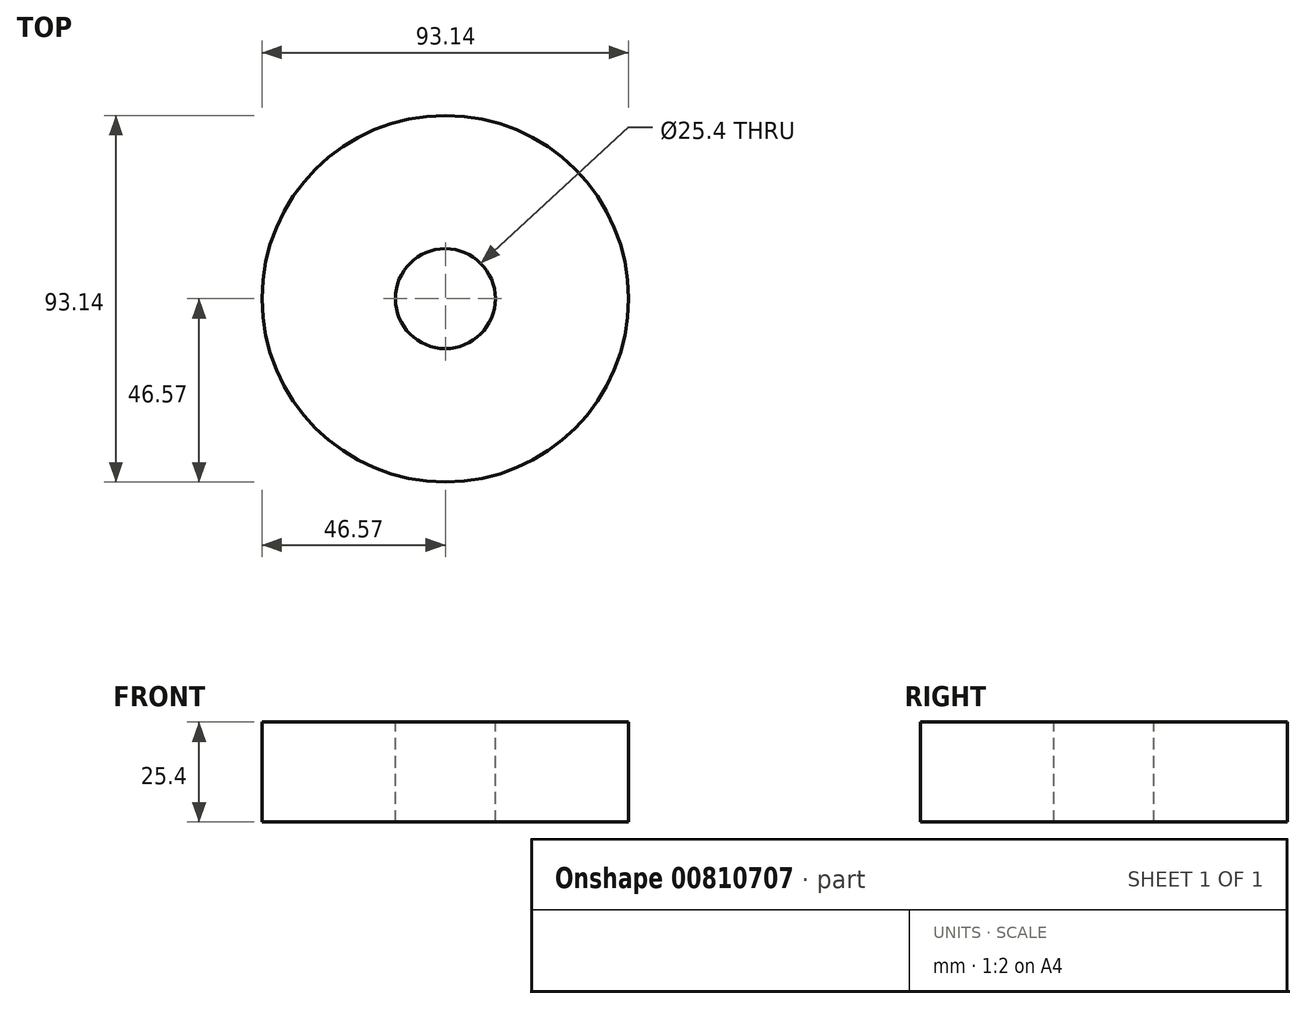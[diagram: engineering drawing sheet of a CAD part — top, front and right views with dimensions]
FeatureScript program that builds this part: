
annotation { "Feature Type Name" : "Feature", "Feature Type Description" : "" }
export const myFeature = defineFeature(function(context is Context, id is Id, definition is map)
    precondition{}
    {
        {
            var Q0;
            Q0=qCreatedBy(makeId("Top.planeOp"),FACE);
            var sketch = newSketch(context, id + "F0", { "sketchPlane" : qUnion([Q0])});
            skCircle(sketch, "E0", {"center": v(0, 0) * mm, "radius": 46.57 * mm});
            skSolve(sketch);
        }
        {
            var Q0;
            Q0 = qSketchRegion(id + "F0", true);
            extrude(context, id + "F1", {"entities" : qUnion([Q0]), "depth" : 25.4 * mm, "offsetDistance" : 25.4 * mm});
        }
        {
            var Q0;
            Q0=qCreatedBy(makeId("Top.planeOp"),FACE);
            var sketch = newSketch(context, id + "F2", { "sketchPlane" : qUnion([Q0])});
            skCircle(sketch, "E1", {"center": v(0, 0) * mm, "radius": 13.73 * mm});
            skSolve(sketch);
        }
        {
            var Q0;
            Q0 = qSketchRegion(id + "F2", true);
            extrude(context, id + "F3", {"entities" : qUnion([Q0]), "operationType" : NewBodyOperationType.ADD, "depth" : 25.4 * mm, "offsetDistance" : 25.4 * mm});
        }
        {
            var Q0;
            Q0=makeQuery(id+"F1.opExtrude","CAP_FACE",FACE,{"disambiguationData":[OSD([sQuery(id+"F0.wireOp",EDGE,"E0")])],"isStart":false});
            var sketch = newSketch(context, id + "F4", { "sketchPlane" : qUnion([Q0])});
            skCircle(sketch, "E2", {"center": v(0, 0) * mm, "radius": 12.7 * mm});
            skSolve(sketch);
        }
        {
            var Q0;
            Q0 = qSketchRegion(id + "F4", true);
            extrude(context, id + "F5", {"entities" : qUnion([Q0]), "operationType" : NewBodyOperationType.ADD, "depth" : 25.4 * mm, "offsetDistance" : 25.4 * mm});
        }
        {
            var Q0;
            Q0=makeQuery(id+"F5.opExtrude","CAP_FACE",FACE,{"disambiguationData":[OSD([sQuery(id+"F4.wireOp",EDGE,"E2")])],"isStart":false});
            extrude(context, id + "F6", {"entities" : qUnion([Q0]), "operationType" : NewBodyOperationType.REMOVE, "oppositeDirection" : true, "depth" : 25.4 * mm, "offsetDistance" : 25.4 * mm});
        }
        {
            var Q0;
            Q0=makeQuery(id+"F6.boolean.opBoolean","MERGE",FACE,{"derivedFrom":[makeQuery(id+"F1.opExtrude","CAP_FACE",FACE,{"disambiguationData":[OSD([sQuery(id+"F0.wireOp",EDGE,"E0")])],"isStart":false}),makeQuery(id+"F6.opExtrude","CAP_FACE",FACE,{"disambiguationData":[OSD([sQuery(id+"F4.wireOp",EDGE,"E2")])],"isStart":false})]});
            var sketch = newSketch(context, id + "F7", { "sketchPlane" : qUnion([Q0])});
            skCircle(sketch, "E3", {"center": v(0, 0) * mm, "radius": 12.7 * mm});
            skSolve(sketch);
        }
        {
            var Q0;
            Q0 = qSketchRegion(id + "F7", true);
            extrude(context, id + "F8", {"entities" : qUnion([Q0]), "operationType" : NewBodyOperationType.REMOVE, "oppositeDirection" : true, "depth" : 25.4 * mm, "offsetDistance" : 25.4 * mm});
        }
    });
